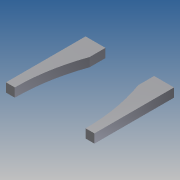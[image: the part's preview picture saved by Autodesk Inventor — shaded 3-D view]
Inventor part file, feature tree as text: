
AUTODESK INVENTOR PART (.ipt)
format: ipt  version: 2015 (Build 190159000, 159)  size: 106,496 bytes
history: native  units: mm
features: extrude x1, sketch x1
ambient origin geometry x8: Origin, YZ Plane, XZ Plane, XY Plane, X Axis, Y Axis, Z Axis, Center Point
bodies: Body1 (feature_tree)
feature tree (2):
  extrude  "Extrusion4"  Depth=1000.0mm
  sketch  "Skizze3"  dims[d4=1000.0mm d5=1000.0mm d6=100.0mm d7=550.0mm d8=180.0mm d9=100.0mm d10=100.0mm d11=320.0mm d12=300.0mm d13=350.0mm d14=230.0mm d15=60.0mm d16=-60.0mm d17=130.0mm d18=190.0mm d19=50.0mm d21=283.537414mm d22=40.0mm d23=140.0mm d24=899.502025mm d25=919.104612mm d26=330.793649mm d31=100.0mm d32=0.0mm]
